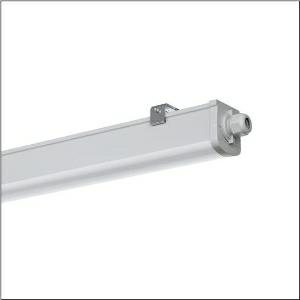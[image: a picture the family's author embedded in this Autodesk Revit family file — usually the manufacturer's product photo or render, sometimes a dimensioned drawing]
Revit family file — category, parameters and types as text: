
# Revit family: monsun_r__31_51fa20dd420b_de40
name_source: partatom
category: Lighting Fixtures
units: mm (PartAtom-declared; Revit-internal decimal feet)

## family parameters
Cut with Voids When Loaded = No
Host = Face
Light Source = No
Part Type = Normal
Room Calculation Point = No
Round Connector Dimension = Use Diameter
Shared = No

## types (1)
- Monsun® 31 (1 x LED, 2300 lm, 19 W, 4000K)
    Apparent Load = 19 VA
    CIE Flux Codes = 42 72 91 92 100
    Color Rendering = 80
    Color Temperature = 4000K
    Default Elevation = 1800 mm
    Description = Monsun® 31, damp-proof luminaire, primary optical cover: diffuser, of PC, frosted, light emission: direct distribution, primary light characteristic: symmetric, installation type: surface-mounted, LED, rated luminous flux: 2.300lm, luminous efficacy: 121lm/W, light colour: 840, colour temperature: 4000K, control gear: DALI 2, with terminal, 5+1-pole, max. 2.5mm², through-wiring: 3x 2.5mm² + 3x 1.5mm², mains connection: 220..240V, AC, 50/60Hz, rated input power: 19W, housing, luminaire housing, of PC, light grey (RAL 7035), length: 558mm, width: 68mm, height: 76mm, protection rating (complete): IP66, insulation class (complete): insulation class II (safety insulation), certification: CE, ENEC, UKCA, protection symbol: D, impact resistance: IK08, permissible operating ambient temperature: -20..+40°C, corresponds to IFS (International Featured Standards) requirements for safety and quality in the food industry, contact your sales advisor before using the luminaires in applications with unclear chemical exposure, large temperature fluctuations or condensation-forming humidity, packaging unit: 1 piece
    Height = 77 mm
    Lamp = 1 x LED
    Lamp Light Flux = 2300 lm
    Lamp Power = 19 W
    Lamp count = 1
    Length = 618 mm
    Luminous efficacy = 121 lm/W
    Manufacturer = Siteco
    ModVariant = No
    Model = 51FA20DD420B
    Mounting Place = Ceiling
    Mounting Type = Surface mounted
    Number of Poles = 1
    OnlyDefault = Yes
    Power Factor = 1
    Product Name = Monsun® 31
    Product group = damp-proof luminaire
    ProductGroupID = 301
    Protection Class = Protection class II
    Protection Degree = IP 66
    RLX_Detail_Level = 1
    RLX_Emergency_Light_Flux = 0 lm
    RLX_Emergency_Type = 0
    RLX_Emergency_Type_DB = No
    RlxData = <blob elided: 32917 chars, md5=fa32b0d3>
    Socket = socket
    Standby Power = 0 W
    System Light Flux = 2300 lm
    System Power = 19 W
    Type Comments = Product without accessories
    Type Image = l_1006174.jpg
    URL = http://relux.com
    VarID = ---
    Voltage = 0 V
    Weight = 0.00 kg
    Width = 69 mm

## geometry (parser evidence)
native form markers: Blend x4, Sweep x13
no freeform markers — native parametric forms only
